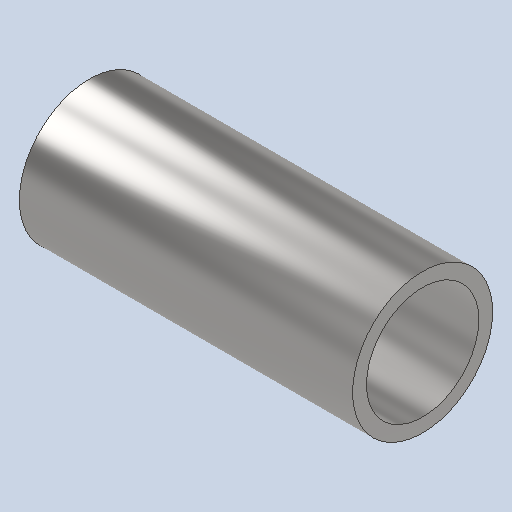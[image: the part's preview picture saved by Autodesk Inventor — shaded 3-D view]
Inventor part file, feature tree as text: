
AUTODESK INVENTOR PART (.ipt)
format: ipt  version: 2022 (Build 260153000, 153)  size: 161,792 bytes
history: native  units: in
note: dims shown in document units (in); Inventor stores cm internally (conversion verified against a paired STEP export)
features: extrude x2, sketch x1
ambient origin geometry x8: Origin, YZ Plane, XZ Plane, XY Plane, X Axis, Y Axis, Z Axis, Center Point
bodies: Solid1 (feature_tree)
feature tree (3):
  extrude  "Extrusion1"  [1 undecoded]
  sketch  "Sketch1"  dims[d0=34.0in d1=0.0in]
  extrude  "Extrude1"  [1 undecoded]
note: 2 required parameter values undecoded (feature->parameter linkage not recoverable at this tier; creation-order binding heuristic only, values carry confidence <= 0.55)
